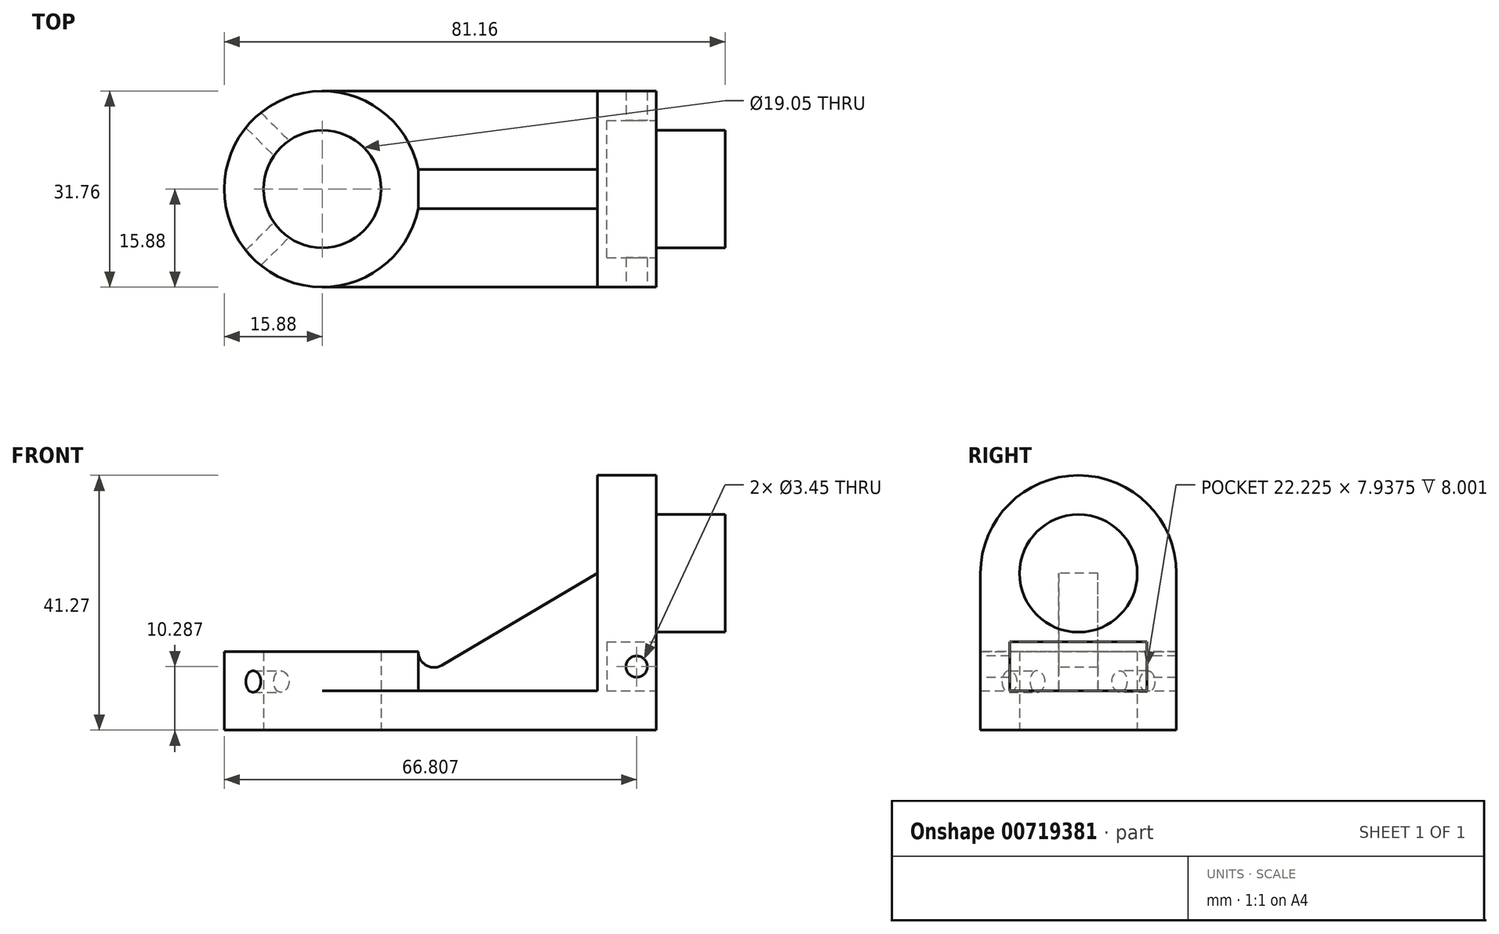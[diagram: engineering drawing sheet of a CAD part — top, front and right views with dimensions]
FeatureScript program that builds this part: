
annotation { "Feature Type Name" : "Feature", "Feature Type Description" : "" }
export const myFeature = defineFeature(function(context is Context, id is Id, definition is map)
    precondition{}
    {
        {
            var Q0;
            Q0=qCreatedBy(makeId("Top.planeOp"),FACE);
            var sketch = newSketch(context, id + "F0", { "sketchPlane" : qUnion([Q0])});
            skCircle(sketch, "E0", {"center": v(0, 0) * mm, "radius": 15.88 * mm});
            skCircle(sketch, "E1", {"center": v(0, 0) * mm, "radius": 9.53 * mm});
            skSolve(sketch);
        }
        {
            var Q0;
            Q0=makeQuery(id+"F0.imprint","IMPRINT",FACE,{"disambiguationData":[TD([[makeQuery(id+"F0.imprint","IMPRINT",EDGE,{"derivedFrom":sQuery(id+"F0.wireOp",EDGE,"E0")}),1.0]])]});
            extrude(context, id + "F1", {"entities" : qUnion([Q0]), "depth" : 12.7 * mm, "offsetDistance" : 25.4 * mm});
        }
        {
            var Q0;
            Q0=qCreatedBy(makeId("Front.planeOp"),FACE);
            var Q1;
            Q1=makeQuery(id+"F1.opExtrude","SWEPT_FACE",FACE,{"disambiguationData":[OSD([sQuery(id+"F0.wireOp",EDGE,"E0")])]});
            cPlane(context, id + "F2", {"entities" : qUnion([Q0, Q1]), "cplaneType" : CPlaneType.LINE_ANGLE, "offset" : 25.4 * mm, "angle" : 45 * degree, "width" : 152.4 * mm, "height" : 152.4 * mm});
        }
        {
            var Q0;
            Q0=qCreatedBy(makeId("Right.planeOp"),FACE);
            var Q1;
            Q1=makeQuery(id+"F1.opExtrude","SWEPT_FACE",FACE,{"disambiguationData":[OSD([sQuery(id+"F0.wireOp",EDGE,"E0")])]});
            cPlane(context, id + "F3", {"entities" : qUnion([Q0, Q1]), "cplaneType" : CPlaneType.LINE_ANGLE, "offset" : 25.4 * mm, "angle" : 45 * degree, "width" : 152.4 * mm, "height" : 152.4 * mm});
        }
        {
            var Q0;
            Q0=qCreatedBy(id+"F2.planeOp",FACE);
            var sketch = newSketch(context, id + "F4", { "sketchPlane" : qUnion([Q0])});
            skCircle(sketch, "E2", {"center": v(0, 7.87) * mm, "radius": 1.73 * mm});
            skLineSegment(sketch, "E3", {"start": v(0, 12.7) * mm, "end": v(0, 0) * mm});
            skSolve(sketch);
        }
        {
            var Q0;
            {var subQ0=sQuery(id+"F4.wireOp",EDGE,"E3");var subQ1=sQuery(id+"F4.wireOp",EDGE,"E2");var subQ2=makeQuery(id+"F4.imprint","INTERSECT",VERTEX,{"disambiguationData":[OD(0.0)],"derivedFrom":[subQ1,subQ0]});Q0=makeQuery(id+"F4.imprint","IMPRINT",FACE,{"disambiguationData":[TD([[makeQuery(id+"F4.imprint","IMPRINT",EDGE,{"disambiguationData":[TD([[subQ2,1.0]])],"derivedFrom":subQ1}),1.0]])]});}
            var Q1;
            {var subQ0=sQuery(id+"F4.wireOp",EDGE,"E3");var subQ1=sQuery(id+"F4.wireOp",EDGE,"E2");var subQ2=makeQuery(id+"F4.imprint","INTERSECT",VERTEX,{"disambiguationData":[OD(0.0)],"derivedFrom":[subQ1,subQ0]});Q1=makeQuery(id+"F4.imprint","IMPRINT",FACE,{"disambiguationData":[TD([[makeQuery(id+"F4.imprint","IMPRINT",EDGE,{"disambiguationData":[TD([[subQ2,-1.0]])],"derivedFrom":subQ1}),1.0]])]});}
            extrude(context, id + "F5", {"entities" : qUnion([Q0, Q1]), "operationType" : NewBodyOperationType.REMOVE, "oppositeDirection" : true, "depth" : 25.4 * mm, "offsetDistance" : 25.4 * mm});
        }
        {
            var Q0;
            Q0=qCreatedBy(id+"F3.planeOp",FACE);
            var sketch = newSketch(context, id + "F6", { "sketchPlane" : qUnion([Q0])});
            skCircle(sketch, "E4", {"center": v(0, 7.87) * mm, "radius": 1.73 * mm});
            skLineSegment(sketch, "E5", {"start": v(0, 0) * mm, "end": v(0, 12.7) * mm});
            skSolve(sketch);
        }
        {
            var Q0;
            Q0 = qSketchRegion(id + "F6", true);
            extrude(context, id + "F7", {"entities" : qUnion([Q0]), "operationType" : NewBodyOperationType.REMOVE, "depth" : 25.4 * mm, "offsetDistance" : 25.4 * mm});
        }
        {
            var Q0;
            Q0=makeQuery(id+"F1.opExtrude","CAP_FACE",FACE,{"disambiguationData":[OSD([sQuery(id+"F0.wireOp",EDGE,"E0"),sQuery(id+"F0.wireOp",EDGE,"E1")])],"isStart":true});
            var sketch = newSketch(context, id + "F8", { "sketchPlane" : qUnion([Q0])});
            skLineSegment(sketch, "E6.bottom", {"start": v(0, 15.88) * mm, "end": v(54.1, 15.88) * mm});
            skLineSegment(sketch, "E6.top", {"start": v(0, -15.88) * mm, "end": v(54.1, -15.88) * mm});
            skLineSegment(sketch, "E6.left", {"start": v(0, 15.88) * mm, "end": v(0, -15.88) * mm});
            skLineSegment(sketch, "E6.right", {"start": v(54.1, 15.88) * mm, "end": v(54.1, -15.88) * mm});
            skSolve(sketch);
        }
        {
            var Q0;
            {var subQ0=sQuery(id+"F8.wireOp",EDGE,"E6.bottom");Q0=makeQuery(id+"F8.imprint","IMPRINT",FACE,{"disambiguationData":[TD([[makeQuery(id+"F8.imprint","IMPRINT",EDGE,{"derivedFrom":subQ0}),-1.0]])]});}
            extrude(context, id + "F9", {"entities" : qUnion([Q0]), "operationType" : NewBodyOperationType.ADD, "oppositeDirection" : true, "depth" : 6.35 * mm, "offsetDistance" : 25.4 * mm});
        }
        {
            var Q0;
            Q0=makeQuery(id+"F9.opExtrude","SWEPT_FACE",FACE,{"disambiguationData":[OSD([sQuery(id+"F8.wireOp",EDGE,"E6.right")])]});
            cPlane(context, id + "F10", {"entities" : qUnion([Q0]), "cplaneType" : CPlaneType.OFFSET, "offset" : 0 * mm, "width" : 152.4 * mm, "height" : 152.4 * mm});
        }
        {
            var Q0;
            Q0=qCreatedBy(id+"F10.planeOp",FACE);
            var sketch = newSketch(context, id + "F11", { "sketchPlane" : qUnion([Q0])});
            skLineSegment(sketch, "E7.bottom", {"start": v(-15.88, 6.35) * mm, "end": v(15.88, 6.35) * mm});
            skLineSegment(sketch, "E7.top", {"start": v(-15.88, 25.4) * mm, "end": v(15.88, 25.4) * mm});
            skLineSegment(sketch, "E7.left", {"start": v(-15.88, 6.35) * mm, "end": v(-15.88, 25.4) * mm});
            skLineSegment(sketch, "E7.right", {"start": v(15.88, 6.35) * mm, "end": v(15.88, 25.4) * mm});
            skArc(sketch, "E8", {"start": v(15.88, 25.4) * mm, "mid": v(0, 41.28) * mm, "end": v(-15.88, 25.4) * mm});
            skSolve(sketch);
        }
        {
            var Q0;
            Q0=makeQuery(id+"F11.imprint","IMPRINT",FACE,{"disambiguationData":[TD([[makeQuery(id+"F11.imprint","IMPRINT",EDGE,{"derivedFrom":sQuery(id+"F11.wireOp",EDGE,"E7.bottom")}),1.0]])]});
            var Q1;
            Q1=makeQuery(id+"F11.imprint","IMPRINT",FACE,{"disambiguationData":[TD([[makeQuery(id+"F11.imprint","IMPRINT",EDGE,{"derivedFrom":sQuery(id+"F11.wireOp",EDGE,"E7.top")}),1.0]])]});
            extrude(context, id + "F12", {"entities" : qUnion([Q0, Q1]), "operationType" : NewBodyOperationType.ADD, "oppositeDirection" : true, "depth" : 9.52 * mm, "offsetDistance" : 25.4 * mm});
        }
        {
            var Q0;
            Q0=makeQuery(id+"F12.opExtrude","CAP_FACE",FACE,{"disambiguationData":[OSD([sQuery(id+"F11.wireOp",EDGE,"E7.bottom"),sQuery(id+"F11.wireOp",EDGE,"E7.left"),sQuery(id+"F11.wireOp",EDGE,"E7.right"),sQuery(id+"F11.wireOp",EDGE,"E8")])],"isStart":false});
            var sketch = newSketch(context, id + "F13", { "sketchPlane" : qUnion([Q0])});
            skLineSegment(sketch, "E9.bottom", {"start": v(-3.18, 6.35) * mm, "end": v(3.18, 6.35) * mm});
            skLineSegment(sketch, "E9.top", {"start": v(-3.18, 25.4) * mm, "end": v(3.18, 25.4) * mm});
            skLineSegment(sketch, "E9.left", {"start": v(-3.18, 6.35) * mm, "end": v(-3.18, 25.4) * mm});
            skLineSegment(sketch, "E9.right", {"start": v(3.17, 6.35) * mm, "end": v(3.17, 25.4) * mm});
            skLineSegment(sketch, "E10", {"start": v(0, 25.4) * mm, "end": v(0, 6.35) * mm});
            skSolve(sketch);
        }
        {
            var Q0;
            Q0 = qSketchRegion(id + "F13", true);
            var Q1;
            Q1=makeQuery(id+"F1.opExtrude","SWEPT_FACE",FACE,{"disambiguationData":[OSD([sQuery(id+"F0.wireOp",EDGE,"E0")])]});
            extrude(context, id + "F14", {"entities" : qUnion([Q0]), "operationType" : NewBodyOperationType.ADD, "endBound" : BoundingType.UP_TO_SURFACE, "depth" : 25.4 * mm, "endBoundEntityFace" : qUnion([Q1]), "offsetDistance" : 25.4 * mm});
        }
        {
            var Q0;
            Q0=makeQuery(id+"F14.opExtrude","SWEPT_FACE",FACE,{"disambiguationData":[OSD([sQuery(id+"F13.wireOp",EDGE,"E9.right")])]});
            var sketch = newSketch(context, id + "F15", { "sketchPlane" : qUnion([Q0])});
            skLineSegment(sketch, "E11", {"start": v(44.58, 25.4) * mm, "end": v(15.55, 25.4) * mm});
            skLineSegment(sketch, "E12", {"start": v(15.55, 25.4) * mm, "end": v(15.55, 12.7) * mm});
            skLineSegment(sketch, "E13", {"start": v(44.58, 25.4) * mm, "end": v(19.39, 10.51) * mm});
            skArc(sketch, "E14", {"start": v(15.55, 12.7) * mm, "mid": v(16.84, 10.5) * mm, "end": v(19.39, 10.51) * mm});
            skSolve(sketch);
        }
        {
            var Q0;
            Q0=makeQuery(id+"F15.imprint","IMPRINT",FACE,{"disambiguationData":[TD([[makeQuery(id+"F15.imprint","IMPRINT",EDGE,{"derivedFrom":sQuery(id+"F15.wireOp",EDGE,"E11")}),-1.0]])]});
            extrude(context, id + "F16", {"entities" : qUnion([Q0]), "operationType" : NewBodyOperationType.REMOVE, "oppositeDirection" : true, "depth" : 25.4 * mm, "offsetDistance" : 25.4 * mm});
        }
        {
            var Q0;
            Q0=makeQuery(id+"F12.boolean.opBoolean","MERGE",FACE,{"derivedFrom":[makeQuery(id+"F9.opExtrude","SWEPT_FACE",FACE,{"disambiguationData":[OSD([sQuery(id+"F8.wireOp",EDGE,"E6.right")])]}),makeQuery(id+"F12.opExtrude","CAP_FACE",FACE,{"disambiguationData":[OSD([sQuery(id+"F11.wireOp",EDGE,"E7.bottom"),sQuery(id+"F11.wireOp",EDGE,"E7.left"),sQuery(id+"F11.wireOp",EDGE,"E7.right"),sQuery(id+"F11.wireOp",EDGE,"E8")])],"isStart":true})]});
            var sketch = newSketch(context, id + "F17", { "sketchPlane" : qUnion([Q0])});
            skCircle(sketch, "E15", {"center": v(0, 25.4) * mm, "radius": 9.53 * mm});
            skSolve(sketch);
        }
        {
            var Q0;
            Q0=makeQuery(id+"F17.imprint","IMPRINT",FACE,{"disambiguationData":[TD([[makeQuery(id+"F17.imprint","IMPRINT",EDGE,{"derivedFrom":sQuery(id+"F17.wireOp",EDGE,"E15")}),1.0]])]});
            extrude(context, id + "F18", {"entities" : qUnion([Q0]), "operationType" : NewBodyOperationType.ADD, "depth" : 11.18 * mm, "offsetDistance" : 25.4 * mm});
        }
        {
            var Q0;
            Q0=makeQuery(id+"F12.boolean.opBoolean","MERGE",FACE,{"derivedFrom":[makeQuery(id+"F9.opExtrude","SWEPT_FACE",FACE,{"disambiguationData":[OSD([sQuery(id+"F8.wireOp",EDGE,"E6.right")])]}),makeQuery(id+"F12.opExtrude","CAP_FACE",FACE,{"disambiguationData":[OSD([sQuery(id+"F11.wireOp",EDGE,"E7.bottom"),sQuery(id+"F11.wireOp",EDGE,"E7.left"),sQuery(id+"F11.wireOp",EDGE,"E7.right"),sQuery(id+"F11.wireOp",EDGE,"E8")])],"isStart":true})]});
            var sketch = newSketch(context, id + "F19", { "sketchPlane" : qUnion([Q0])});
            skLineSegment(sketch, "E16.bottom", {"start": v(-11.11, 14.29) * mm, "end": v(11.11, 14.29) * mm});
            skLineSegment(sketch, "E16.top", {"start": v(-11.11, 6.35) * mm, "end": v(11.11, 6.35) * mm});
            skLineSegment(sketch, "E16.left", {"start": v(-11.11, 14.29) * mm, "end": v(-11.11, 6.35) * mm});
            skLineSegment(sketch, "E16.right", {"start": v(11.11, 14.29) * mm, "end": v(11.11, 6.35) * mm});
            skSolve(sketch);
        }
        {
            var Q0;
            Q0=makeQuery(id+"F19.imprint","IMPRINT",FACE,{"disambiguationData":[TD([[makeQuery(id+"F19.imprint","IMPRINT",EDGE,{"derivedFrom":sQuery(id+"F19.wireOp",EDGE,"E16.bottom")}),-1.0]])]});
            extrude(context, id + "F20", {"entities" : qUnion([Q0]), "operationType" : NewBodyOperationType.REMOVE, "oppositeDirection" : true, "depth" : 8 * mm, "offsetDistance" : 25.4 * mm});
        }
        {
            var Q0;
            Q0=makeQuery(id+"F12.boolean.opBoolean","MERGE",FACE,{"derivedFrom":[makeQuery(id+"F9.opExtrude","SWEPT_FACE",FACE,{"disambiguationData":[OSD([sQuery(id+"F8.wireOp",EDGE,"E6.bottom")])]}),makeQuery(id+"F12.opExtrude","SWEPT_FACE",FACE,{"disambiguationData":[OSD([sQuery(id+"F11.wireOp",EDGE,"E7.left")])]})]});
            var sketch = newSketch(context, id + "F21", { "sketchPlane" : qUnion([Q0])});
            skCircle(sketch, "E17", {"center": v(50.93, 10.29) * mm, "radius": 1.73 * mm});
            skSolve(sketch);
        }
        {
            var Q0;
            Q0=makeQuery(id+"F21.imprint","IMPRINT",FACE,{"disambiguationData":[TD([[makeQuery(id+"F21.imprint","IMPRINT",EDGE,{"derivedFrom":sQuery(id+"F21.wireOp",EDGE,"E17")}),1.0]])]});
            extrude(context, id + "F22", {"entities" : qUnion([Q0]), "operationType" : NewBodyOperationType.REMOVE, "oppositeDirection" : true, "depth" : 101.6 * mm, "offsetDistance" : 25.4 * mm});
        }
    });
